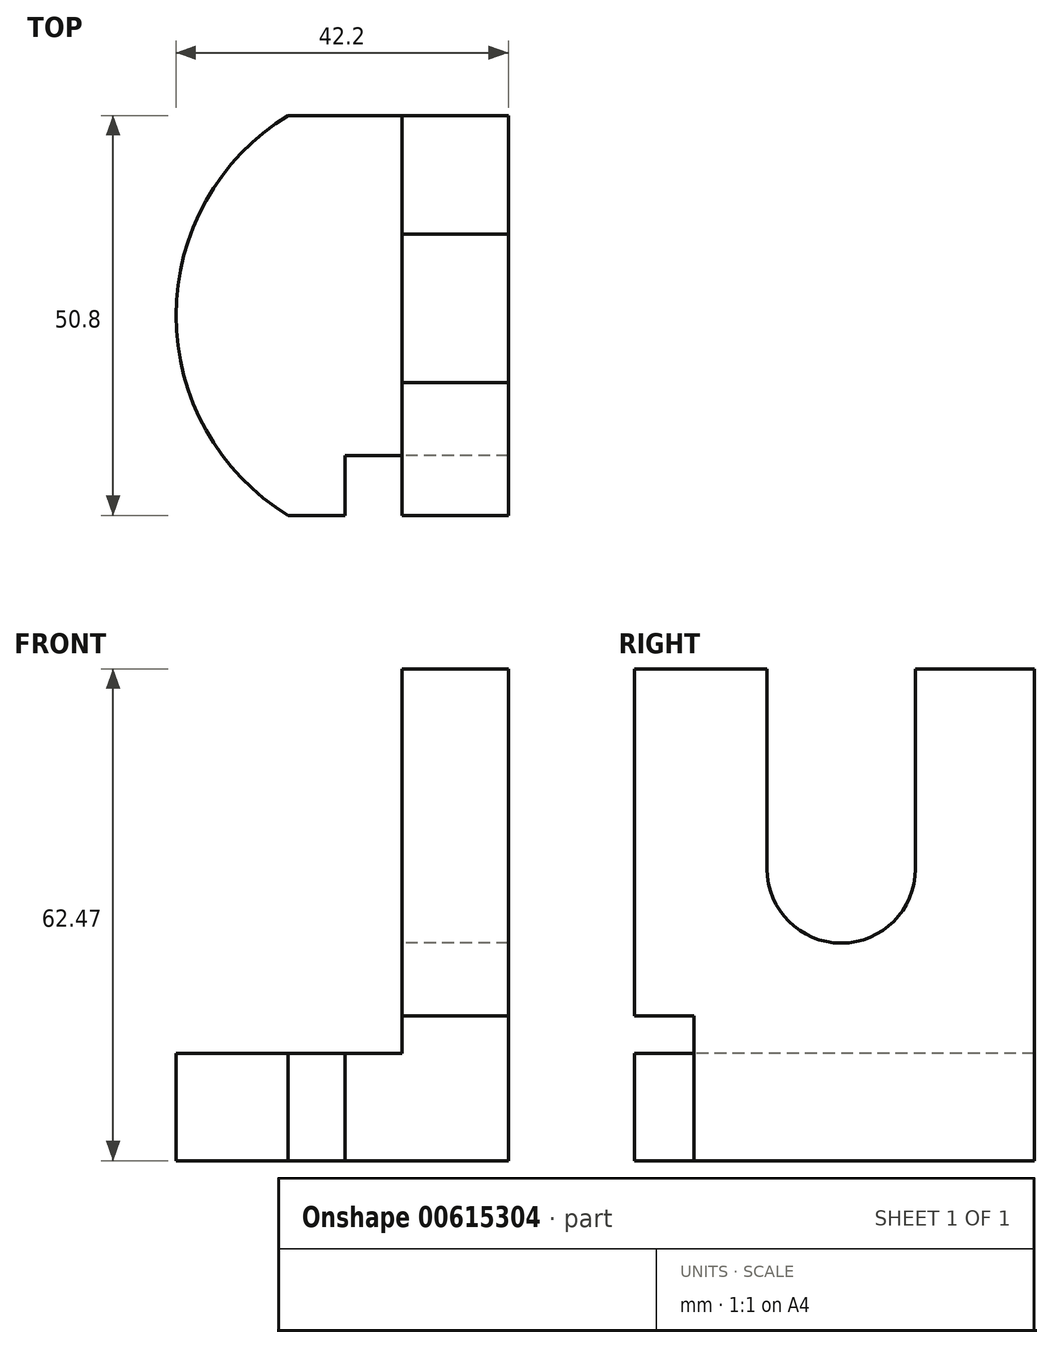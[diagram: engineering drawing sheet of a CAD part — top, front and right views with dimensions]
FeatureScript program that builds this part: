
annotation { "Feature Type Name" : "Feature", "Feature Type Description" : "" }
export const myFeature = defineFeature(function(context is Context, id is Id, definition is map)
    precondition{}
    {
        {
            var Q0;
            Q0=qCreatedBy(makeId("Front.planeOp"),FACE);
            var sketch = newSketch(context, id + "F0", { "sketchPlane" : qUnion([Q0])});
            skLineSegment(sketch, "E0", {"start": v(0, 0) * mm, "end": v(0, 62.47) * mm});
            skLineSegment(sketch, "E1", {"start": v(0, 62.47) * mm, "end": v(-13.49, 62.47) * mm});
            skLineSegment(sketch, "E2", {"start": v(-13.49, 62.47) * mm, "end": v(-13.49, 13.63) * mm});
            skLineSegment(sketch, "E3", {"start": v(-13.49, 13.63) * mm, "end": v(-42.45, 13.63) * mm});
            skLineSegment(sketch, "E4", {"start": v(-42.45, 13.63) * mm, "end": v(-42.45, 0) * mm});
            skLineSegment(sketch, "E5", {"start": v(-42.45, 0) * mm, "end": v(0, 0) * mm});
            skSolve(sketch);
        }
        {
            var Q0;
            Q0 = qSketchRegion(id + "F0", true);
            extrude(context, id + "F1", {"entities" : qUnion([Q0]), "oppositeDirection" : true, "depth" : 50.8 * mm, "offsetDistance" : 25.4 * mm});
        }
        {
            var Q0;
            Q0=makeQuery(id+"F1.opExtrude","SWEPT_FACE",FACE,{"disambiguationData":[OSD([sQuery(id+"F0.wireOp",EDGE,"E3")])]});
            var sketch = newSketch(context, id + "F2", { "sketchPlane" : qUnion([Q0])});
            skArc(sketch, "E6", {"start": v(-27.97, 50.8) * mm, "mid": v(-42.2, 25.4) * mm, "end": v(-27.97, 0) * mm});
            skSolve(sketch);
        }
        {
            var Q0;
            {var subQ0=sQuery(id+"F2.wireOp",EDGE,"E6");Q0=makeQuery(id+"F2.imprint","IMPRINT",FACE,{"disambiguationData":[TD([[makeQuery(id+"F2.imprint","IMPRINT",EDGE,{"derivedFrom":subQ0}),-1.0]])]});}
            extrude(context, id + "F3", {"entities" : qUnion([Q0]), "operationType" : NewBodyOperationType.REMOVE, "oppositeDirection" : true, "depth" : 25.4 * mm, "offsetDistance" : 25.4 * mm});
        }
        {
            var Q0;
            Q0=makeQuery(id+"F1.opExtrude","CAP_FACE",FACE,{"disambiguationData":[OSD([sQuery(id+"F0.wireOp",EDGE,"E0"),sQuery(id+"F0.wireOp",EDGE,"E1"),sQuery(id+"F0.wireOp",EDGE,"E2"),sQuery(id+"F0.wireOp",EDGE,"E3"),sQuery(id+"F0.wireOp",EDGE,"E4"),sQuery(id+"F0.wireOp",EDGE,"E5")])],"isStart":true});
            var sketch = newSketch(context, id + "F4", { "sketchPlane" : qUnion([Q0])});
            skLineSegment(sketch, "E7.bottom", {"start": v(5.32, -2.3) * mm, "end": v(-20.72, -2.3) * mm});
            skLineSegment(sketch, "E7.top", {"start": v(5.32, 18.36) * mm, "end": v(-20.72, 18.36) * mm});
            skLineSegment(sketch, "E7.left", {"start": v(5.32, -2.3) * mm, "end": v(5.32, 18.36) * mm});
            skLineSegment(sketch, "E7.right", {"start": v(-20.72, -2.3) * mm, "end": v(-20.72, 18.36) * mm});
            skSolve(sketch);
        }
        {
            var Q0;
            Q0 = qSketchRegion(id + "F4", true);
            extrude(context, id + "F5", {"entities" : qUnion([Q0]), "operationType" : NewBodyOperationType.REMOVE, "oppositeDirection" : true, "depth" : 7.62 * mm, "offsetDistance" : 25.4 * mm});
        }
        {
            var Q0;
            Q0=makeQuery(id+"F1.opExtrude","SWEPT_FACE",FACE,{"disambiguationData":[OSD([sQuery(id+"F0.wireOp",EDGE,"E1")])]});
            var sketch = newSketch(context, id + "F6", { "sketchPlane" : qUnion([Q0])});
            skLineSegment(sketch, "E8", {"start": v(0, 25.4) * mm, "end": v(0, 35.73) * mm});
            skLineSegment(sketch, "E9", {"start": v(0, 35.73) * mm, "end": v(-13.49, 35.73) * mm});
            skLineSegment(sketch, "E10", {"start": v(-13.49, 35.73) * mm, "end": v(-13.49, 16.87) * mm});
            skLineSegment(sketch, "E11", {"start": v(-13.49, 16.87) * mm, "end": v(0, 16.87) * mm});
            skLineSegment(sketch, "E12", {"start": v(0, 16.87) * mm, "end": v(0, 25.4) * mm});
            skSolve(sketch);
        }
        {
            var Q0;
            Q0=makeQuery(id+"F6.imprint","IMPRINT",FACE,{"disambiguationData":[TD([[makeQuery(id+"F6.imprint","IMPRINT",EDGE,{"derivedFrom":sQuery(id+"F6.wireOp",EDGE,"E8")}),-1.0]])]});
            extrude(context, id + "F7", {"entities" : qUnion([Q0]), "operationType" : NewBodyOperationType.REMOVE, "oppositeDirection" : true, "depth" : 25.4 * mm, "offsetDistance" : 25.4 * mm});
        }
        {
            var Q0;
            Q0=makeQuery(id+"F1.opExtrude","SWEPT_FACE",FACE,{"disambiguationData":[OSD([sQuery(id+"F0.wireOp",EDGE,"E2")])]});
            var sketch = newSketch(context, id + "F8", { "sketchPlane" : qUnion([Q0])});
            skArc(sketch, "E13", {"start": v(-35.73, 37.07) * mm, "mid": v(-26.3, 27.64) * mm, "end": v(-16.87, 37.07) * mm});
            skSolve(sketch);
        }
        {
            var Q0;
            Q0=makeQuery(id+"F8.imprint","IMPRINT",FACE,{"disambiguationData":[TD([[makeQuery(id+"F8.imprint","IMPRINT",EDGE,{"derivedFrom":sQuery(id+"F8.wireOp",EDGE,"E13")}),1.0]])]});
            extrude(context, id + "F9", {"entities" : qUnion([Q0]), "operationType" : NewBodyOperationType.REMOVE, "oppositeDirection" : true, "depth" : 25.4 * mm, "offsetDistance" : 25.4 * mm});
        }
    });
